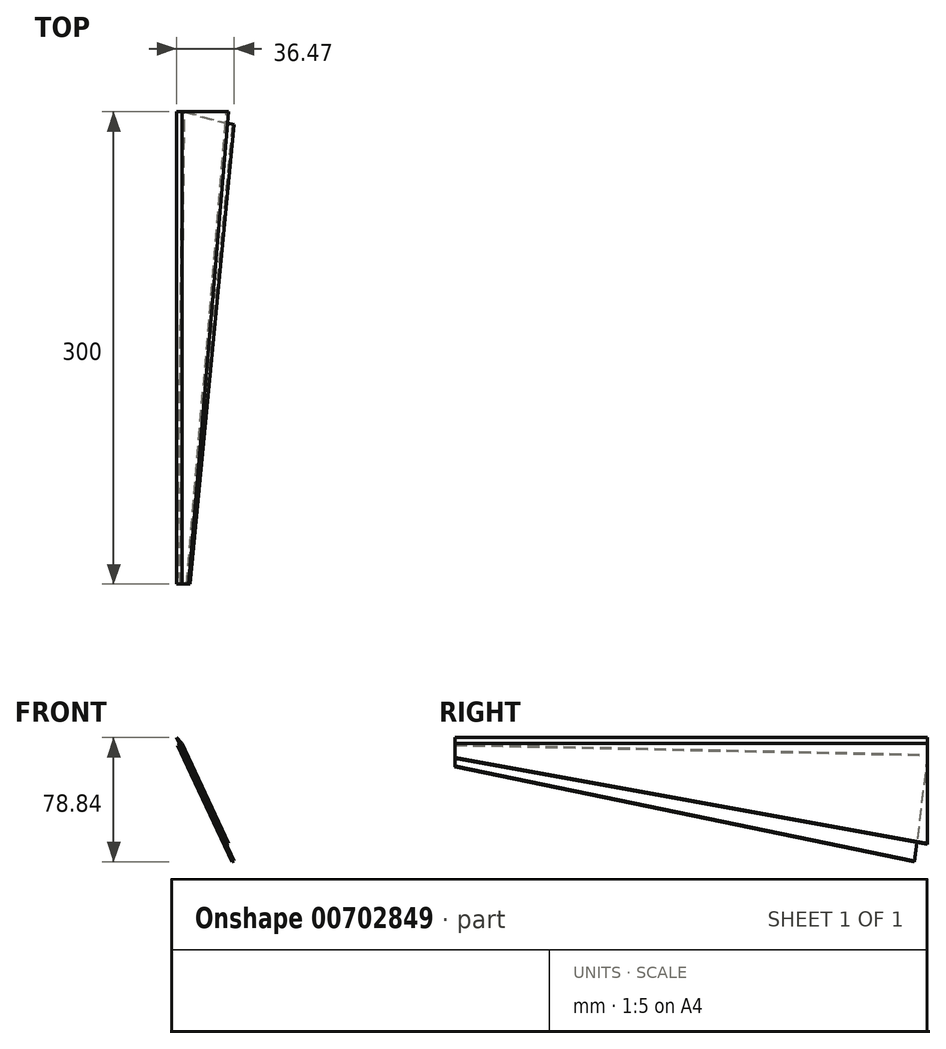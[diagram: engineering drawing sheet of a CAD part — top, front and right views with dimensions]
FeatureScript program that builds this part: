
annotation { "Feature Type Name" : "Feature", "Feature Type Description" : "" }
export const myFeature = defineFeature(function(context is Context, id is Id, definition is map)
    precondition{}
    {
        {
            var Q0;
            Q0=qCreatedBy(makeId("Top.planeOp"),FACE);
            var sketch = newSketch(context, id + "F0", { "sketchPlane" : qUnion([Q0])});
            skLineSegment(sketch, "E0", {"start": v(0, -64.28) * mm, "end": v(0, 68.4) * mm, "construction": true});
            skLineSegment(sketch, "E1.0", {"start": v(2, -150) * mm, "end": v(2, 150) * mm});
            skLineSegment(sketch, "E2.0", {"start": v(-2, -150) * mm, "end": v(-2, 150) * mm, "construction": true});
            skLineSegment(sketch, "E3", {"start": v(-9.81, 0) * mm, "end": v(10.1, 0) * mm, "construction": true});
            skSolve(sketch);
        }
        {
            var Q0;
            Q0=sQuery(id+"F0.wireOp",EDGE,"E1.0");
            var Q1;
            Q1=qCreatedBy(makeId("Right.planeOp"),FACE);
            cPlane(context, id + "F1", {"entities" : qUnion([Q0, Q1]), "cplaneType" : CPlaneType.LINE_ANGLE, "offset" : 25 * mm, "angle" : 25 * degree, "oppositeDirection" : true, "width" : 150 * mm, "height" : 150 * mm});
        }
        {
            var Q0;
            Q0=qCreatedBy(id+"F1.planeOp",FACE);
            var sketch = newSketch(context, id + "F2", { "sketchPlane" : qUnion([Q0])});
            skLineSegment(sketch, "E4.0", {"start": v(150, -0.85) * mm, "end": v(-150, -0.85) * mm});
            skLineSegment(sketch, "E5", {"start": v(150, -15.85) * mm, "end": v(-150, -75.85) * mm});
            skLineSegment(sketch, "E6", {"start": v(-150, -75.85) * mm, "end": v(-150, -0.85) * mm});
            skLineSegment(sketch, "E7", {"start": v(-150, -12.9) * mm, "end": v(-141.79, -87.44) * mm});
            skLineSegment(sketch, "E8", {"start": v(-141.79, -87.44) * mm, "end": v(150, -20.85) * mm});
            skLineSegment(sketch, "E9", {"start": v(150, -20.85) * mm, "end": v(150, -5.85) * mm});
            skLineSegment(sketch, "E10", {"start": v(150, -5.85) * mm, "end": v(-150, -12.9) * mm});
            skLineSegment(sketch, "E11", {"start": v(150, -0.85) * mm, "end": v(150, -15.85) * mm});
            skSolve(sketch);
        }
        {
            var Q0;
            {var subQ0=sQuery(id+"F2.wireOp",EDGE,"E4.0");Q0=makeQuery(id+"F2.imprint","IMPRINT",FACE,{"disambiguationData":[TD([[makeQuery(id+"F2.imprint","IMPRINT",EDGE,{"derivedFrom":subQ0}),1.0]])]});}
            var Q1;
            {var subQ0=sQuery(id+"F2.wireOp",EDGE,"E6");var subQ1=sQuery(id+"F2.wireOp",EDGE,"E5");var subQ2=makeQuery(id+"F2.imprint","INTERSECT",VERTEX,{"derivedFrom":[subQ1,subQ0]});Q1=makeQuery(id+"F2.imprint","IMPRINT",FACE,{"disambiguationData":[TD([[makeQuery(id+"F2.imprint","IMPRINT",EDGE,{"disambiguationData":[TD([[subQ2,1.0]])],"derivedFrom":subQ1}),-1.0]])]});}
            var Q2;
            {var subQ5=sQuery(id+"F2.wireOp",EDGE,"E10");Q2=makeQuery(id+"F2.imprint","IMPRINT",FACE,{"disambiguationData":[TD([[makeQuery(id+"F2.imprint","IMPRINT",EDGE,{"derivedFrom":subQ5}),1.0]])]});}
            extrude(context, id + "F3", {"entities" : qUnion([Q0, Q1, Q2]), "oppositeDirection" : true, "depth" : 1.5 * mm, "offsetDistance" : 25 * mm});
        }
        {
            var Q0;
            {var subQ5=sQuery(id+"F2.wireOp",EDGE,"E8");Q0=makeQuery(id+"F2.imprint","IMPRINT",FACE,{"disambiguationData":[TD([[makeQuery(id+"F2.imprint","IMPRINT",EDGE,{"derivedFrom":subQ5}),1.0]])]});}
            var Q1;
            {var subQ5=sQuery(id+"F2.wireOp",EDGE,"E10");Q1=makeQuery(id+"F2.imprint","IMPRINT",FACE,{"disambiguationData":[TD([[makeQuery(id+"F2.imprint","IMPRINT",EDGE,{"derivedFrom":subQ5}),1.0]])]});}
            extrude(context, id + "F4", {"entities" : qUnion([Q0, Q1]), "depth" : 1.5 * mm, "offsetDistance" : 25 * mm});
        }
        {
            var Q0;
            Q0=makeQuery(id+"F3.opExtrude","CAP_EDGE",EDGE,{"disambiguationData":[OSD([sQuery(id+"F2.wireOp",EDGE,"E4.0")])],"isStart":false});
            chamfer(context, id + "F5", {"entities" : qUnion([Q0]), "chamferType" : ChamferType.TWO_OFFSETS, "width1" : 1.6 * mm, "oppositeDirection" : false, "width2" : 5 * mm, "tangentPropagation" : true});
        }
    });
